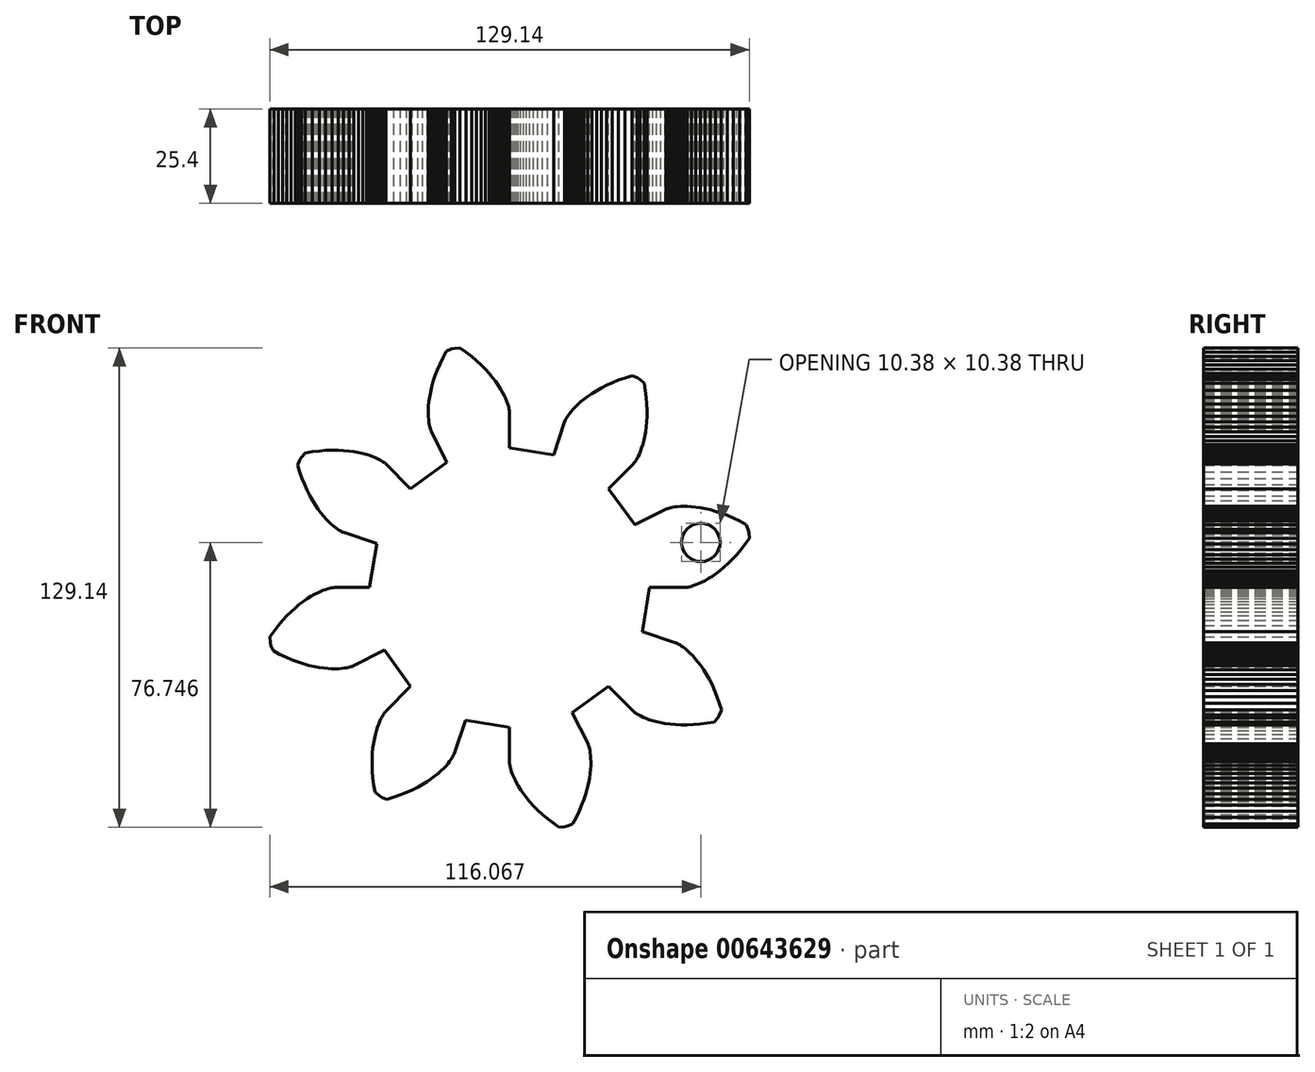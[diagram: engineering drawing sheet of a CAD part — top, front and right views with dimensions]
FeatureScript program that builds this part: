
annotation { "Feature Type Name" : "Feature", "Feature Type Description" : "" }
export const myFeature = defineFeature(function(context is Context, id is Id, definition is map)
    precondition{}
    {
        {
            var Q0;
            Q0=qCreatedBy(makeId("Front.planeOp"),FACE);
            var sketch = newSketch(context, id + "F0", { "sketchPlane" : qUnion([Q0])});
            skLineSegment(sketch, "E0", {"start": v(37.7, 0) * mm, "end": v(47.16, 0) * mm});
            skLineSegment(sketch, "E1", {"start": v(47.16, 0) * mm, "end": v(47.24, 0) * mm});
            skLineSegment(sketch, "E2", {"start": v(47.24, 0) * mm, "end": v(47.4, 0.02) * mm});
            skLineSegment(sketch, "E3", {"start": v(47.4, 0.02) * mm, "end": v(47.67, 0.05) * mm});
            skLineSegment(sketch, "E4", {"start": v(47.67, 0.05) * mm, "end": v(48, 0.11) * mm});
            skLineSegment(sketch, "E5", {"start": v(48, 0.11) * mm, "end": v(48.44, 0.2) * mm});
            skLineSegment(sketch, "E6", {"start": v(48.44, 0.2) * mm, "end": v(48.95, 0.34) * mm});
            skLineSegment(sketch, "E7", {"start": v(48.95, 0.34) * mm, "end": v(49.54, 0.52) * mm});
            skLineSegment(sketch, "E8", {"start": v(49.54, 0.52) * mm, "end": v(50.21, 0.76) * mm});
            skLineSegment(sketch, "E9", {"start": v(50.21, 0.76) * mm, "end": v(50.95, 1.07) * mm});
            skLineSegment(sketch, "E10", {"start": v(50.95, 1.07) * mm, "end": v(51.76, 1.44) * mm});
            skLineSegment(sketch, "E11", {"start": v(51.76, 1.44) * mm, "end": v(52.63, 1.89) * mm});
            skLineSegment(sketch, "E12", {"start": v(52.63, 1.89) * mm, "end": v(53.55, 2.42) * mm});
            skLineSegment(sketch, "E13", {"start": v(53.55, 2.42) * mm, "end": v(54.53, 3.04) * mm});
            skLineSegment(sketch, "E14", {"start": v(54.53, 3.04) * mm, "end": v(55.56, 3.75) * mm});
            skLineSegment(sketch, "E15", {"start": v(55.56, 3.75) * mm, "end": v(56.62, 4.56) * mm});
            skLineSegment(sketch, "E16", {"start": v(56.62, 4.56) * mm, "end": v(57.72, 5.47) * mm});
            skLineSegment(sketch, "E17", {"start": v(57.72, 5.47) * mm, "end": v(58.84, 6.49) * mm});
            skLineSegment(sketch, "E18", {"start": v(58.84, 6.49) * mm, "end": v(59.98, 7.62) * mm});
            skLineSegment(sketch, "E19", {"start": v(59.98, 7.62) * mm, "end": v(61.13, 8.87) * mm});
            skLineSegment(sketch, "E20", {"start": v(61.13, 8.87) * mm, "end": v(62.29, 10.23) * mm});
            skLineSegment(sketch, "E21", {"start": v(62.29, 10.23) * mm, "end": v(63.44, 11.71) * mm});
            skLineSegment(sketch, "E22", {"start": v(63.44, 11.71) * mm, "end": v(64.57, 13.32) * mm});
            skLineSegment(sketch, "E23", {"start": v(64.57, 13.32) * mm, "end": v(64.48, 14.77) * mm});
            skLineSegment(sketch, "E24", {"start": v(64.48, 14.77) * mm, "end": v(64.26, 15.67) * mm});
            skLineSegment(sketch, "E25", {"start": v(64.26, 15.67) * mm, "end": v(63.7, 17.01) * mm});
            skLineSegment(sketch, "E26", {"start": v(63.7, 17.01) * mm, "end": v(61.96, 17.94) * mm});
            skLineSegment(sketch, "E27", {"start": v(61.96, 17.94) * mm, "end": v(60.27, 18.75) * mm});
            skLineSegment(sketch, "E28", {"start": v(60.27, 18.75) * mm, "end": v(58.63, 19.45) * mm});
            skLineSegment(sketch, "E29", {"start": v(58.63, 19.45) * mm, "end": v(57.04, 20.05) * mm});
            skLineSegment(sketch, "E30", {"start": v(57.04, 20.05) * mm, "end": v(55.52, 20.55) * mm});
            skLineSegment(sketch, "E31", {"start": v(55.52, 20.55) * mm, "end": v(54.06, 20.96) * mm});
            skLineSegment(sketch, "E32", {"start": v(54.06, 20.96) * mm, "end": v(52.67, 21.29) * mm});
            skLineSegment(sketch, "E33", {"start": v(52.67, 21.29) * mm, "end": v(51.35, 21.53) * mm});
            skLineSegment(sketch, "E34", {"start": v(51.35, 21.53) * mm, "end": v(50.12, 21.7) * mm});
            skLineSegment(sketch, "E35", {"start": v(50.12, 21.7) * mm, "end": v(48.96, 21.82) * mm});
            skLineSegment(sketch, "E36", {"start": v(48.96, 21.82) * mm, "end": v(47.9, 21.88) * mm});
            skLineSegment(sketch, "E37", {"start": v(47.9, 21.88) * mm, "end": v(46.92, 21.9) * mm});
            skLineSegment(sketch, "E38", {"start": v(46.92, 21.9) * mm, "end": v(46.03, 21.87) * mm});
            skLineSegment(sketch, "E39", {"start": v(46.03, 21.87) * mm, "end": v(45.24, 21.8) * mm});
            skLineSegment(sketch, "E40", {"start": v(45.24, 21.8) * mm, "end": v(44.53, 21.72) * mm});
            skLineSegment(sketch, "E41", {"start": v(44.53, 21.72) * mm, "end": v(43.92, 21.62) * mm});
            skLineSegment(sketch, "E42", {"start": v(43.92, 21.62) * mm, "end": v(43.4, 21.51) * mm});
            skLineSegment(sketch, "E43", {"start": v(43.4, 21.51) * mm, "end": v(42.98, 21.4) * mm});
            skLineSegment(sketch, "E44", {"start": v(42.98, 21.4) * mm, "end": v(42.64, 21.3) * mm});
            skLineSegment(sketch, "E45", {"start": v(42.64, 21.3) * mm, "end": v(42.4, 21.22) * mm});
            skLineSegment(sketch, "E46", {"start": v(42.4, 21.22) * mm, "end": v(42.24, 21.15) * mm});
            skLineSegment(sketch, "E47", {"start": v(42.24, 21.15) * mm, "end": v(42.16, 21.12) * mm});
            skLineSegment(sketch, "E48", {"start": v(42.16, 21.12) * mm, "end": v(33.71, 16.89) * mm});
            skLineSegment(sketch, "E49", {"start": v(33.71, 16.89) * mm, "end": v(26.66, 26.66) * mm});
            skLineSegment(sketch, "E50", {"start": v(26.66, 26.66) * mm, "end": v(33.34, 33.34) * mm});
            skLineSegment(sketch, "E51", {"start": v(33.34, 33.34) * mm, "end": v(33.4, 33.4) * mm});
            skLineSegment(sketch, "E52", {"start": v(33.4, 33.4) * mm, "end": v(33.5, 33.53) * mm});
            skLineSegment(sketch, "E53", {"start": v(33.5, 33.53) * mm, "end": v(33.67, 33.74) * mm});
            skLineSegment(sketch, "E54", {"start": v(33.67, 33.74) * mm, "end": v(33.87, 34.03) * mm});
            skLineSegment(sketch, "E55", {"start": v(33.87, 34.03) * mm, "end": v(34.1, 34.4) * mm});
            skLineSegment(sketch, "E56", {"start": v(34.1, 34.4) * mm, "end": v(34.37, 34.85) * mm});
            skLineSegment(sketch, "E57", {"start": v(34.37, 34.85) * mm, "end": v(34.66, 35.4) * mm});
            skLineSegment(sketch, "E58", {"start": v(34.66, 35.4) * mm, "end": v(34.97, 36.04) * mm});
            skLineSegment(sketch, "E59", {"start": v(34.97, 36.04) * mm, "end": v(35.27, 36.78) * mm});
            skLineSegment(sketch, "E60", {"start": v(35.27, 36.78) * mm, "end": v(35.58, 37.62) * mm});
            skLineSegment(sketch, "E61", {"start": v(35.58, 37.62) * mm, "end": v(35.88, 38.55) * mm});
            skLineSegment(sketch, "E62", {"start": v(35.88, 38.55) * mm, "end": v(36.16, 39.58) * mm});
            skLineSegment(sketch, "E63", {"start": v(36.16, 39.58) * mm, "end": v(36.41, 40.7) * mm});
            skLineSegment(sketch, "E64", {"start": v(36.41, 40.7) * mm, "end": v(36.64, 41.93) * mm});
            skLineSegment(sketch, "E65", {"start": v(36.64, 41.93) * mm, "end": v(36.82, 43.26) * mm});
            skLineSegment(sketch, "E66", {"start": v(36.82, 43.26) * mm, "end": v(36.95, 44.68) * mm});
            skLineSegment(sketch, "E67", {"start": v(36.95, 44.68) * mm, "end": v(37.02, 46.2) * mm});
            skLineSegment(sketch, "E68", {"start": v(37.02, 46.2) * mm, "end": v(37.03, 47.8) * mm});
            skLineSegment(sketch, "E69", {"start": v(37.03, 47.8) * mm, "end": v(36.96, 49.5) * mm});
            skLineSegment(sketch, "E70", {"start": v(36.96, 49.5) * mm, "end": v(36.81, 51.28) * mm});
            skLineSegment(sketch, "E71", {"start": v(36.81, 51.28) * mm, "end": v(36.57, 53.14) * mm});
            skLineSegment(sketch, "E72", {"start": v(36.57, 53.14) * mm, "end": v(36.24, 55.08) * mm});
            skLineSegment(sketch, "E73", {"start": v(36.24, 55.08) * mm, "end": v(35.15, 56.04) * mm});
            skLineSegment(sketch, "E74", {"start": v(35.15, 56.04) * mm, "end": v(34.36, 56.52) * mm});
            skLineSegment(sketch, "E75", {"start": v(34.36, 56.52) * mm, "end": v(33.01, 57.07) * mm});
            skLineSegment(sketch, "E76", {"start": v(33.01, 57.07) * mm, "end": v(31.13, 56.5) * mm});
            skLineSegment(sketch, "E77", {"start": v(31.13, 56.5) * mm, "end": v(29.36, 55.88) * mm});
            skLineSegment(sketch, "E78", {"start": v(29.36, 55.88) * mm, "end": v(27.7, 55.21) * mm});
            skLineSegment(sketch, "E79", {"start": v(27.7, 55.21) * mm, "end": v(26.16, 54.51) * mm});
            skLineSegment(sketch, "E80", {"start": v(26.16, 54.51) * mm, "end": v(24.72, 53.79) * mm});
            skLineSegment(sketch, "E81", {"start": v(24.72, 53.79) * mm, "end": v(23.4, 53.04) * mm});
            skLineSegment(sketch, "E82", {"start": v(23.4, 53.04) * mm, "end": v(22.2, 52.3) * mm});
            skLineSegment(sketch, "E83", {"start": v(22.2, 52.3) * mm, "end": v(21.09, 51.54) * mm});
            skLineSegment(sketch, "E84", {"start": v(21.09, 51.54) * mm, "end": v(20.09, 50.79) * mm});
            skLineSegment(sketch, "E85", {"start": v(20.09, 50.79) * mm, "end": v(19.2, 50.05) * mm});
            skLineSegment(sketch, "E86", {"start": v(19.2, 50.05) * mm, "end": v(18.4, 49.34) * mm});
            skLineSegment(sketch, "E87", {"start": v(18.4, 49.34) * mm, "end": v(17.7, 48.66) * mm});
            skLineSegment(sketch, "E88", {"start": v(17.7, 48.66) * mm, "end": v(17.09, 48.01) * mm});
            skLineSegment(sketch, "E89", {"start": v(17.09, 48.01) * mm, "end": v(16.57, 47.4) * mm});
            skLineSegment(sketch, "E90", {"start": v(16.57, 47.4) * mm, "end": v(16.13, 46.85) * mm});
            skLineSegment(sketch, "E91", {"start": v(16.13, 46.85) * mm, "end": v(15.77, 46.34) * mm});
            skLineSegment(sketch, "E92", {"start": v(15.77, 46.34) * mm, "end": v(15.48, 45.9) * mm});
            skLineSegment(sketch, "E93", {"start": v(15.48, 45.9) * mm, "end": v(15.25, 45.52) * mm});
            skLineSegment(sketch, "E94", {"start": v(15.25, 45.52) * mm, "end": v(15.09, 45.21) * mm});
            skLineSegment(sketch, "E95", {"start": v(15.09, 45.21) * mm, "end": v(14.98, 44.98) * mm});
            skLineSegment(sketch, "E96", {"start": v(14.98, 44.98) * mm, "end": v(14.9, 44.82) * mm});
            skLineSegment(sketch, "E97", {"start": v(14.9, 44.82) * mm, "end": v(14.88, 44.75) * mm});
            skLineSegment(sketch, "E98", {"start": v(14.88, 44.75) * mm, "end": v(11.9, 35.78) * mm});
            skLineSegment(sketch, "E99", {"start": v(11.9, 35.78) * mm, "end": v(0, 37.7) * mm});
            skLineSegment(sketch, "E100", {"start": v(0, 37.7) * mm, "end": v(0, 47.16) * mm});
            skLineSegment(sketch, "E101", {"start": v(0, 47.16) * mm, "end": v(0, 47.24) * mm});
            skLineSegment(sketch, "E102", {"start": v(0, 47.24) * mm, "end": v(-0.02, 47.4) * mm});
            skLineSegment(sketch, "E103", {"start": v(-0.02, 47.4) * mm, "end": v(-0.05, 47.67) * mm});
            skLineSegment(sketch, "E104", {"start": v(-0.05, 47.67) * mm, "end": v(-0.11, 48) * mm});
            skLineSegment(sketch, "E105", {"start": v(-0.11, 48) * mm, "end": v(-0.2, 48.44) * mm});
            skLineSegment(sketch, "E106", {"start": v(-0.2, 48.44) * mm, "end": v(-0.34, 48.95) * mm});
            skLineSegment(sketch, "E107", {"start": v(-0.34, 48.95) * mm, "end": v(-0.52, 49.54) * mm});
            skLineSegment(sketch, "E108", {"start": v(-0.52, 49.54) * mm, "end": v(-0.76, 50.21) * mm});
            skLineSegment(sketch, "E109", {"start": v(-0.76, 50.21) * mm, "end": v(-1.07, 50.95) * mm});
            skLineSegment(sketch, "E110", {"start": v(-1.07, 50.95) * mm, "end": v(-1.44, 51.76) * mm});
            skLineSegment(sketch, "E111", {"start": v(-1.44, 51.76) * mm, "end": v(-1.89, 52.63) * mm});
            skLineSegment(sketch, "E112", {"start": v(-1.89, 52.63) * mm, "end": v(-2.42, 53.55) * mm});
            skLineSegment(sketch, "E113", {"start": v(-2.42, 53.55) * mm, "end": v(-3.04, 54.53) * mm});
            skLineSegment(sketch, "E114", {"start": v(-3.04, 54.53) * mm, "end": v(-3.75, 55.56) * mm});
            skLineSegment(sketch, "E115", {"start": v(-3.75, 55.56) * mm, "end": v(-4.56, 56.62) * mm});
            skLineSegment(sketch, "E116", {"start": v(-4.56, 56.62) * mm, "end": v(-5.47, 57.72) * mm});
            skLineSegment(sketch, "E117", {"start": v(-5.47, 57.72) * mm, "end": v(-6.49, 58.84) * mm});
            skLineSegment(sketch, "E118", {"start": v(-6.49, 58.84) * mm, "end": v(-7.62, 59.98) * mm});
            skLineSegment(sketch, "E119", {"start": v(-7.62, 59.98) * mm, "end": v(-8.87, 61.13) * mm});
            skLineSegment(sketch, "E120", {"start": v(-8.87, 61.13) * mm, "end": v(-10.23, 62.29) * mm});
            skLineSegment(sketch, "E121", {"start": v(-10.23, 62.29) * mm, "end": v(-11.71, 63.44) * mm});
            skLineSegment(sketch, "E122", {"start": v(-11.71, 63.44) * mm, "end": v(-13.32, 64.57) * mm});
            skLineSegment(sketch, "E123", {"start": v(-13.32, 64.57) * mm, "end": v(-14.77, 64.48) * mm});
            skLineSegment(sketch, "E124", {"start": v(-14.77, 64.48) * mm, "end": v(-15.67, 64.26) * mm});
            skLineSegment(sketch, "E125", {"start": v(-15.67, 64.26) * mm, "end": v(-17.01, 63.7) * mm});
            skLineSegment(sketch, "E126", {"start": v(-17.01, 63.7) * mm, "end": v(-17.94, 61.96) * mm});
            skLineSegment(sketch, "E127", {"start": v(-17.94, 61.96) * mm, "end": v(-18.75, 60.27) * mm});
            skLineSegment(sketch, "E128", {"start": v(-18.75, 60.27) * mm, "end": v(-19.45, 58.63) * mm});
            skLineSegment(sketch, "E129", {"start": v(-19.45, 58.63) * mm, "end": v(-20.05, 57.04) * mm});
            skLineSegment(sketch, "E130", {"start": v(-20.05, 57.04) * mm, "end": v(-20.55, 55.52) * mm});
            skLineSegment(sketch, "E131", {"start": v(-20.55, 55.52) * mm, "end": v(-20.96, 54.06) * mm});
            skLineSegment(sketch, "E132", {"start": v(-20.96, 54.06) * mm, "end": v(-21.29, 52.67) * mm});
            skLineSegment(sketch, "E133", {"start": v(-21.29, 52.67) * mm, "end": v(-21.53, 51.35) * mm});
            skLineSegment(sketch, "E134", {"start": v(-21.53, 51.35) * mm, "end": v(-21.7, 50.12) * mm});
            skLineSegment(sketch, "E135", {"start": v(-21.7, 50.12) * mm, "end": v(-21.82, 48.96) * mm});
            skLineSegment(sketch, "E136", {"start": v(-21.82, 48.96) * mm, "end": v(-21.88, 47.9) * mm});
            skLineSegment(sketch, "E137", {"start": v(-21.88, 47.9) * mm, "end": v(-21.9, 46.92) * mm});
            skLineSegment(sketch, "E138", {"start": v(-21.9, 46.92) * mm, "end": v(-21.87, 46.03) * mm});
            skLineSegment(sketch, "E139", {"start": v(-21.87, 46.03) * mm, "end": v(-21.8, 45.24) * mm});
            skLineSegment(sketch, "E140", {"start": v(-21.8, 45.24) * mm, "end": v(-21.72, 44.53) * mm});
            skLineSegment(sketch, "E141", {"start": v(-21.72, 44.53) * mm, "end": v(-21.62, 43.92) * mm});
            skLineSegment(sketch, "E142", {"start": v(-21.62, 43.92) * mm, "end": v(-21.51, 43.4) * mm});
            skLineSegment(sketch, "E143", {"start": v(-21.51, 43.4) * mm, "end": v(-21.4, 42.98) * mm});
            skLineSegment(sketch, "E144", {"start": v(-21.4, 42.98) * mm, "end": v(-21.3, 42.64) * mm});
            skLineSegment(sketch, "E145", {"start": v(-21.3, 42.64) * mm, "end": v(-21.22, 42.4) * mm});
            skLineSegment(sketch, "E146", {"start": v(-21.22, 42.4) * mm, "end": v(-21.15, 42.24) * mm});
            skLineSegment(sketch, "E147", {"start": v(-21.15, 42.24) * mm, "end": v(-21.12, 42.16) * mm});
            skLineSegment(sketch, "E148", {"start": v(-21.12, 42.16) * mm, "end": v(-16.89, 33.71) * mm});
            skLineSegment(sketch, "E149", {"start": v(-16.89, 33.71) * mm, "end": v(-26.66, 26.66) * mm});
            skLineSegment(sketch, "E150", {"start": v(-26.66, 26.66) * mm, "end": v(-33.34, 33.34) * mm});
            skLineSegment(sketch, "E151", {"start": v(-33.34, 33.34) * mm, "end": v(-33.4, 33.4) * mm});
            skLineSegment(sketch, "E152", {"start": v(-33.4, 33.4) * mm, "end": v(-33.53, 33.5) * mm});
            skLineSegment(sketch, "E153", {"start": v(-33.53, 33.5) * mm, "end": v(-33.74, 33.67) * mm});
            skLineSegment(sketch, "E154", {"start": v(-33.74, 33.67) * mm, "end": v(-34.03, 33.87) * mm});
            skLineSegment(sketch, "E155", {"start": v(-34.03, 33.87) * mm, "end": v(-34.4, 34.1) * mm});
            skLineSegment(sketch, "E156", {"start": v(-34.4, 34.1) * mm, "end": v(-34.85, 34.37) * mm});
            skLineSegment(sketch, "E157", {"start": v(-34.85, 34.37) * mm, "end": v(-35.4, 34.66) * mm});
            skLineSegment(sketch, "E158", {"start": v(-35.4, 34.66) * mm, "end": v(-36.04, 34.97) * mm});
            skLineSegment(sketch, "E159", {"start": v(-36.04, 34.97) * mm, "end": v(-36.78, 35.27) * mm});
            skLineSegment(sketch, "E160", {"start": v(-36.78, 35.27) * mm, "end": v(-37.61, 35.58) * mm});
            skLineSegment(sketch, "E161", {"start": v(-37.61, 35.58) * mm, "end": v(-38.55, 35.88) * mm});
            skLineSegment(sketch, "E162", {"start": v(-38.55, 35.88) * mm, "end": v(-39.58, 36.16) * mm});
            skLineSegment(sketch, "E163", {"start": v(-39.58, 36.16) * mm, "end": v(-40.7, 36.41) * mm});
            skLineSegment(sketch, "E164", {"start": v(-40.7, 36.41) * mm, "end": v(-41.93, 36.64) * mm});
            skLineSegment(sketch, "E165", {"start": v(-41.93, 36.64) * mm, "end": v(-43.26, 36.82) * mm});
            skLineSegment(sketch, "E166", {"start": v(-43.26, 36.82) * mm, "end": v(-44.68, 36.95) * mm});
            skLineSegment(sketch, "E167", {"start": v(-44.68, 36.95) * mm, "end": v(-46.2, 37.02) * mm});
            skLineSegment(sketch, "E168", {"start": v(-46.2, 37.02) * mm, "end": v(-47.8, 37.03) * mm});
            skLineSegment(sketch, "E169", {"start": v(-47.8, 37.03) * mm, "end": v(-49.5, 36.96) * mm});
            skLineSegment(sketch, "E170", {"start": v(-49.5, 36.96) * mm, "end": v(-51.28, 36.81) * mm});
            skLineSegment(sketch, "E171", {"start": v(-51.28, 36.81) * mm, "end": v(-53.14, 36.57) * mm});
            skLineSegment(sketch, "E172", {"start": v(-53.14, 36.57) * mm, "end": v(-55.08, 36.24) * mm});
            skLineSegment(sketch, "E173", {"start": v(-55.08, 36.24) * mm, "end": v(-56.04, 35.15) * mm});
            skLineSegment(sketch, "E174", {"start": v(-56.04, 35.15) * mm, "end": v(-56.52, 34.36) * mm});
            skLineSegment(sketch, "E175", {"start": v(-56.52, 34.36) * mm, "end": v(-57.07, 33.01) * mm});
            skLineSegment(sketch, "E176", {"start": v(-57.07, 33.01) * mm, "end": v(-56.5, 31.13) * mm});
            skLineSegment(sketch, "E177", {"start": v(-56.5, 31.13) * mm, "end": v(-55.88, 29.36) * mm});
            skLineSegment(sketch, "E178", {"start": v(-55.88, 29.36) * mm, "end": v(-55.21, 27.7) * mm});
            skLineSegment(sketch, "E179", {"start": v(-55.21, 27.7) * mm, "end": v(-54.51, 26.16) * mm});
            skLineSegment(sketch, "E180", {"start": v(-54.51, 26.16) * mm, "end": v(-53.79, 24.72) * mm});
            skLineSegment(sketch, "E181", {"start": v(-53.79, 24.72) * mm, "end": v(-53.04, 23.4) * mm});
            skLineSegment(sketch, "E182", {"start": v(-53.04, 23.4) * mm, "end": v(-52.3, 22.2) * mm});
            skLineSegment(sketch, "E183", {"start": v(-52.3, 22.2) * mm, "end": v(-51.54, 21.09) * mm});
            skLineSegment(sketch, "E184", {"start": v(-51.54, 21.09) * mm, "end": v(-50.79, 20.09) * mm});
            skLineSegment(sketch, "E185", {"start": v(-50.79, 20.09) * mm, "end": v(-50.05, 19.2) * mm});
            skLineSegment(sketch, "E186", {"start": v(-50.05, 19.2) * mm, "end": v(-49.34, 18.4) * mm});
            skLineSegment(sketch, "E187", {"start": v(-49.34, 18.4) * mm, "end": v(-48.66, 17.7) * mm});
            skLineSegment(sketch, "E188", {"start": v(-48.66, 17.7) * mm, "end": v(-48.01, 17.09) * mm});
            skLineSegment(sketch, "E189", {"start": v(-48.01, 17.09) * mm, "end": v(-47.4, 16.57) * mm});
            skLineSegment(sketch, "E190", {"start": v(-47.4, 16.57) * mm, "end": v(-46.85, 16.13) * mm});
            skLineSegment(sketch, "E191", {"start": v(-46.85, 16.13) * mm, "end": v(-46.34, 15.77) * mm});
            skLineSegment(sketch, "E192", {"start": v(-46.34, 15.77) * mm, "end": v(-45.9, 15.48) * mm});
            skLineSegment(sketch, "E193", {"start": v(-45.9, 15.48) * mm, "end": v(-45.52, 15.25) * mm});
            skLineSegment(sketch, "E194", {"start": v(-45.52, 15.25) * mm, "end": v(-45.21, 15.09) * mm});
            skLineSegment(sketch, "E195", {"start": v(-45.21, 15.09) * mm, "end": v(-44.98, 14.98) * mm});
            skLineSegment(sketch, "E196", {"start": v(-44.98, 14.98) * mm, "end": v(-44.82, 14.9) * mm});
            skLineSegment(sketch, "E197", {"start": v(-44.82, 14.9) * mm, "end": v(-44.75, 14.88) * mm});
            skLineSegment(sketch, "E198", {"start": v(-44.75, 14.88) * mm, "end": v(-35.78, 11.9) * mm});
            skLineSegment(sketch, "E199", {"start": v(-35.78, 11.9) * mm, "end": v(-37.7, 0) * mm});
            skLineSegment(sketch, "E200", {"start": v(-37.7, 0) * mm, "end": v(-47.16, 0) * mm});
            skLineSegment(sketch, "E201", {"start": v(-47.16, 0) * mm, "end": v(-47.24, 0) * mm});
            skLineSegment(sketch, "E202", {"start": v(-47.24, 0) * mm, "end": v(-47.4, -0.02) * mm});
            skLineSegment(sketch, "E203", {"start": v(-47.4, -0.02) * mm, "end": v(-47.66, -0.05) * mm});
            skLineSegment(sketch, "E204", {"start": v(-47.66, -0.05) * mm, "end": v(-48, -0.11) * mm});
            skLineSegment(sketch, "E205", {"start": v(-48, -0.11) * mm, "end": v(-48.44, -0.2) * mm});
            skLineSegment(sketch, "E206", {"start": v(-48.44, -0.2) * mm, "end": v(-48.95, -0.34) * mm});
            skLineSegment(sketch, "E207", {"start": v(-48.95, -0.34) * mm, "end": v(-49.54, -0.52) * mm});
            skLineSegment(sketch, "E208", {"start": v(-49.54, -0.52) * mm, "end": v(-50.21, -0.76) * mm});
            skLineSegment(sketch, "E209", {"start": v(-50.21, -0.76) * mm, "end": v(-50.95, -1.07) * mm});
            skLineSegment(sketch, "E210", {"start": v(-50.95, -1.07) * mm, "end": v(-51.76, -1.44) * mm});
            skLineSegment(sketch, "E211", {"start": v(-51.76, -1.44) * mm, "end": v(-52.63, -1.89) * mm});
            skLineSegment(sketch, "E212", {"start": v(-52.63, -1.89) * mm, "end": v(-53.55, -2.42) * mm});
            skLineSegment(sketch, "E213", {"start": v(-53.55, -2.42) * mm, "end": v(-54.53, -3.04) * mm});
            skLineSegment(sketch, "E214", {"start": v(-54.53, -3.04) * mm, "end": v(-55.56, -3.75) * mm});
            skLineSegment(sketch, "E215", {"start": v(-55.56, -3.75) * mm, "end": v(-56.62, -4.56) * mm});
            skLineSegment(sketch, "E216", {"start": v(-56.62, -4.56) * mm, "end": v(-57.72, -5.47) * mm});
            skLineSegment(sketch, "E217", {"start": v(-57.72, -5.47) * mm, "end": v(-58.84, -6.49) * mm});
            skLineSegment(sketch, "E218", {"start": v(-58.84, -6.49) * mm, "end": v(-59.98, -7.62) * mm});
            skLineSegment(sketch, "E219", {"start": v(-59.98, -7.62) * mm, "end": v(-61.13, -8.87) * mm});
            skLineSegment(sketch, "E220", {"start": v(-61.13, -8.87) * mm, "end": v(-62.29, -10.23) * mm});
            skLineSegment(sketch, "E221", {"start": v(-62.29, -10.23) * mm, "end": v(-63.44, -11.71) * mm});
            skLineSegment(sketch, "E222", {"start": v(-63.44, -11.71) * mm, "end": v(-64.57, -13.32) * mm});
            skLineSegment(sketch, "E223", {"start": v(-64.57, -13.32) * mm, "end": v(-64.48, -14.77) * mm});
            skLineSegment(sketch, "E224", {"start": v(-64.48, -14.77) * mm, "end": v(-64.26, -15.67) * mm});
            skLineSegment(sketch, "E225", {"start": v(-64.26, -15.67) * mm, "end": v(-63.7, -17.01) * mm});
            skLineSegment(sketch, "E226", {"start": v(-63.7, -17.01) * mm, "end": v(-61.96, -17.94) * mm});
            skLineSegment(sketch, "E227", {"start": v(-61.96, -17.94) * mm, "end": v(-60.27, -18.75) * mm});
            skLineSegment(sketch, "E228", {"start": v(-60.27, -18.75) * mm, "end": v(-58.63, -19.45) * mm});
            skLineSegment(sketch, "E229", {"start": v(-58.63, -19.45) * mm, "end": v(-57.04, -20.05) * mm});
            skLineSegment(sketch, "E230", {"start": v(-57.04, -20.05) * mm, "end": v(-55.52, -20.55) * mm});
            skLineSegment(sketch, "E231", {"start": v(-55.52, -20.55) * mm, "end": v(-54.06, -20.96) * mm});
            skLineSegment(sketch, "E232", {"start": v(-54.06, -20.96) * mm, "end": v(-52.67, -21.29) * mm});
            skLineSegment(sketch, "E233", {"start": v(-52.67, -21.29) * mm, "end": v(-51.35, -21.53) * mm});
            skLineSegment(sketch, "E234", {"start": v(-51.35, -21.53) * mm, "end": v(-50.12, -21.7) * mm});
            skLineSegment(sketch, "E235", {"start": v(-50.12, -21.7) * mm, "end": v(-48.96, -21.82) * mm});
            skLineSegment(sketch, "E236", {"start": v(-48.96, -21.82) * mm, "end": v(-47.9, -21.88) * mm});
            skLineSegment(sketch, "E237", {"start": v(-47.9, -21.88) * mm, "end": v(-46.92, -21.9) * mm});
            skLineSegment(sketch, "E238", {"start": v(-46.92, -21.9) * mm, "end": v(-46.03, -21.87) * mm});
            skLineSegment(sketch, "E239", {"start": v(-46.03, -21.87) * mm, "end": v(-45.24, -21.8) * mm});
            skLineSegment(sketch, "E240", {"start": v(-45.24, -21.8) * mm, "end": v(-44.53, -21.72) * mm});
            skLineSegment(sketch, "E241", {"start": v(-44.53, -21.72) * mm, "end": v(-43.92, -21.62) * mm});
            skLineSegment(sketch, "E242", {"start": v(-43.92, -21.62) * mm, "end": v(-43.4, -21.51) * mm});
            skLineSegment(sketch, "E243", {"start": v(-43.4, -21.51) * mm, "end": v(-42.98, -21.4) * mm});
            skLineSegment(sketch, "E244", {"start": v(-42.98, -21.4) * mm, "end": v(-42.64, -21.3) * mm});
            skLineSegment(sketch, "E245", {"start": v(-42.64, -21.3) * mm, "end": v(-42.4, -21.22) * mm});
            skLineSegment(sketch, "E246", {"start": v(-42.4, -21.22) * mm, "end": v(-42.24, -21.15) * mm});
            skLineSegment(sketch, "E247", {"start": v(-42.24, -21.15) * mm, "end": v(-42.16, -21.12) * mm});
            skLineSegment(sketch, "E248", {"start": v(-42.16, -21.12) * mm, "end": v(-33.71, -16.89) * mm});
            skLineSegment(sketch, "E249", {"start": v(-33.71, -16.89) * mm, "end": v(-26.66, -26.66) * mm});
            skLineSegment(sketch, "E250", {"start": v(-26.66, -26.66) * mm, "end": v(-33.34, -33.34) * mm});
            skLineSegment(sketch, "E251", {"start": v(-33.34, -33.34) * mm, "end": v(-33.4, -33.4) * mm});
            skLineSegment(sketch, "E252", {"start": v(-33.4, -33.4) * mm, "end": v(-33.5, -33.53) * mm});
            skLineSegment(sketch, "E253", {"start": v(-33.5, -33.53) * mm, "end": v(-33.67, -33.74) * mm});
            skLineSegment(sketch, "E254", {"start": v(-33.67, -33.74) * mm, "end": v(-33.87, -34.03) * mm});
            skLineSegment(sketch, "E255", {"start": v(-33.87, -34.03) * mm, "end": v(-34.1, -34.4) * mm});
            skLineSegment(sketch, "E256", {"start": v(-34.1, -34.4) * mm, "end": v(-34.37, -34.85) * mm});
            skLineSegment(sketch, "E257", {"start": v(-34.37, -34.85) * mm, "end": v(-34.66, -35.4) * mm});
            skLineSegment(sketch, "E258", {"start": v(-34.66, -35.4) * mm, "end": v(-34.96, -36.04) * mm});
            skLineSegment(sketch, "E259", {"start": v(-34.96, -36.04) * mm, "end": v(-35.27, -36.78) * mm});
            skLineSegment(sketch, "E260", {"start": v(-35.27, -36.78) * mm, "end": v(-35.58, -37.61) * mm});
            skLineSegment(sketch, "E261", {"start": v(-35.58, -37.61) * mm, "end": v(-35.88, -38.55) * mm});
            skLineSegment(sketch, "E262", {"start": v(-35.88, -38.55) * mm, "end": v(-36.16, -39.58) * mm});
            skLineSegment(sketch, "E263", {"start": v(-36.16, -39.58) * mm, "end": v(-36.41, -40.7) * mm});
            skLineSegment(sketch, "E264", {"start": v(-36.41, -40.7) * mm, "end": v(-36.64, -41.93) * mm});
            skLineSegment(sketch, "E265", {"start": v(-36.64, -41.93) * mm, "end": v(-36.82, -43.26) * mm});
            skLineSegment(sketch, "E266", {"start": v(-36.82, -43.26) * mm, "end": v(-36.95, -44.68) * mm});
            skLineSegment(sketch, "E267", {"start": v(-36.95, -44.68) * mm, "end": v(-37.02, -46.2) * mm});
            skLineSegment(sketch, "E268", {"start": v(-37.02, -46.2) * mm, "end": v(-37.03, -47.8) * mm});
            skLineSegment(sketch, "E269", {"start": v(-37.03, -47.8) * mm, "end": v(-36.96, -49.5) * mm});
            skLineSegment(sketch, "E270", {"start": v(-36.96, -49.5) * mm, "end": v(-36.81, -51.28) * mm});
            skLineSegment(sketch, "E271", {"start": v(-36.81, -51.28) * mm, "end": v(-36.57, -53.14) * mm});
            skLineSegment(sketch, "E272", {"start": v(-36.57, -53.14) * mm, "end": v(-36.24, -55.08) * mm});
            skLineSegment(sketch, "E273", {"start": v(-36.24, -55.08) * mm, "end": v(-35.15, -56.04) * mm});
            skLineSegment(sketch, "E274", {"start": v(-35.15, -56.04) * mm, "end": v(-34.36, -56.52) * mm});
            skLineSegment(sketch, "E275", {"start": v(-34.36, -56.52) * mm, "end": v(-33.01, -57.07) * mm});
            skLineSegment(sketch, "E276", {"start": v(-33.01, -57.07) * mm, "end": v(-31.13, -56.5) * mm});
            skLineSegment(sketch, "E277", {"start": v(-31.13, -56.5) * mm, "end": v(-29.36, -55.88) * mm});
            skLineSegment(sketch, "E278", {"start": v(-29.36, -55.88) * mm, "end": v(-27.7, -55.21) * mm});
            skLineSegment(sketch, "E279", {"start": v(-27.7, -55.21) * mm, "end": v(-26.16, -54.51) * mm});
            skLineSegment(sketch, "E280", {"start": v(-26.16, -54.51) * mm, "end": v(-24.72, -53.79) * mm});
            skLineSegment(sketch, "E281", {"start": v(-24.72, -53.79) * mm, "end": v(-23.4, -53.04) * mm});
            skLineSegment(sketch, "E282", {"start": v(-23.4, -53.04) * mm, "end": v(-22.2, -52.3) * mm});
            skLineSegment(sketch, "E283", {"start": v(-22.2, -52.3) * mm, "end": v(-21.09, -51.54) * mm});
            skLineSegment(sketch, "E284", {"start": v(-21.09, -51.54) * mm, "end": v(-20.09, -50.79) * mm});
            skLineSegment(sketch, "E285", {"start": v(-20.09, -50.79) * mm, "end": v(-19.2, -50.05) * mm});
            skLineSegment(sketch, "E286", {"start": v(-19.2, -50.05) * mm, "end": v(-18.4, -49.34) * mm});
            skLineSegment(sketch, "E287", {"start": v(-18.4, -49.34) * mm, "end": v(-17.7, -48.66) * mm});
            skLineSegment(sketch, "E288", {"start": v(-17.7, -48.66) * mm, "end": v(-17.09, -48.01) * mm});
            skLineSegment(sketch, "E289", {"start": v(-17.09, -48.01) * mm, "end": v(-16.57, -47.4) * mm});
            skLineSegment(sketch, "E290", {"start": v(-16.57, -47.4) * mm, "end": v(-16.13, -46.85) * mm});
            skLineSegment(sketch, "E291", {"start": v(-16.13, -46.85) * mm, "end": v(-15.77, -46.34) * mm});
            skLineSegment(sketch, "E292", {"start": v(-15.77, -46.34) * mm, "end": v(-15.48, -45.9) * mm});
            skLineSegment(sketch, "E293", {"start": v(-15.48, -45.9) * mm, "end": v(-15.25, -45.52) * mm});
            skLineSegment(sketch, "E294", {"start": v(-15.25, -45.52) * mm, "end": v(-15.09, -45.21) * mm});
            skLineSegment(sketch, "E295", {"start": v(-15.09, -45.21) * mm, "end": v(-14.97, -44.98) * mm});
            skLineSegment(sketch, "E296", {"start": v(-14.97, -44.98) * mm, "end": v(-14.9, -44.82) * mm});
            skLineSegment(sketch, "E297", {"start": v(-14.9, -44.82) * mm, "end": v(-14.88, -44.75) * mm});
            skLineSegment(sketch, "E298", {"start": v(-14.88, -44.75) * mm, "end": v(-11.9, -35.78) * mm});
            skLineSegment(sketch, "E299", {"start": v(-11.9, -35.78) * mm, "end": v(0, -37.7) * mm});
            skLineSegment(sketch, "E300", {"start": v(0, -37.7) * mm, "end": v(0, -47.16) * mm});
            skLineSegment(sketch, "E301", {"start": v(0, -47.16) * mm, "end": v(0, -47.24) * mm});
            skLineSegment(sketch, "E302", {"start": v(0, -47.24) * mm, "end": v(0.02, -47.4) * mm});
            skLineSegment(sketch, "E303", {"start": v(0.02, -47.4) * mm, "end": v(0.05, -47.66) * mm});
            skLineSegment(sketch, "E304", {"start": v(0.05, -47.66) * mm, "end": v(0.11, -48) * mm});
            skLineSegment(sketch, "E305", {"start": v(0.11, -48) * mm, "end": v(0.2, -48.44) * mm});
            skLineSegment(sketch, "E306", {"start": v(0.2, -48.44) * mm, "end": v(0.34, -48.95) * mm});
            skLineSegment(sketch, "E307", {"start": v(0.34, -48.95) * mm, "end": v(0.52, -49.54) * mm});
            skLineSegment(sketch, "E308", {"start": v(0.52, -49.54) * mm, "end": v(0.76, -50.21) * mm});
            skLineSegment(sketch, "E309", {"start": v(0.76, -50.21) * mm, "end": v(1.07, -50.95) * mm});
            skLineSegment(sketch, "E310", {"start": v(1.07, -50.95) * mm, "end": v(1.44, -51.76) * mm});
            skLineSegment(sketch, "E311", {"start": v(1.44, -51.76) * mm, "end": v(1.89, -52.63) * mm});
            skLineSegment(sketch, "E312", {"start": v(1.89, -52.63) * mm, "end": v(2.42, -53.55) * mm});
            skLineSegment(sketch, "E313", {"start": v(2.42, -53.55) * mm, "end": v(3.04, -54.53) * mm});
            skLineSegment(sketch, "E314", {"start": v(3.04, -54.53) * mm, "end": v(3.75, -55.56) * mm});
            skLineSegment(sketch, "E315", {"start": v(3.75, -55.56) * mm, "end": v(4.56, -56.62) * mm});
            skLineSegment(sketch, "E316", {"start": v(4.56, -56.62) * mm, "end": v(5.47, -57.72) * mm});
            skLineSegment(sketch, "E317", {"start": v(5.47, -57.72) * mm, "end": v(6.49, -58.84) * mm});
            skLineSegment(sketch, "E318", {"start": v(6.49, -58.84) * mm, "end": v(7.62, -59.98) * mm});
            skLineSegment(sketch, "E319", {"start": v(7.62, -59.98) * mm, "end": v(8.87, -61.13) * mm});
            skLineSegment(sketch, "E320", {"start": v(8.87, -61.13) * mm, "end": v(10.23, -62.29) * mm});
            skLineSegment(sketch, "E321", {"start": v(10.23, -62.29) * mm, "end": v(11.71, -63.44) * mm});
            skLineSegment(sketch, "E322", {"start": v(11.71, -63.44) * mm, "end": v(13.32, -64.57) * mm});
            skLineSegment(sketch, "E323", {"start": v(13.32, -64.57) * mm, "end": v(14.77, -64.48) * mm});
            skLineSegment(sketch, "E324", {"start": v(14.77, -64.48) * mm, "end": v(15.67, -64.26) * mm});
            skLineSegment(sketch, "E325", {"start": v(15.67, -64.26) * mm, "end": v(17.01, -63.7) * mm});
            skLineSegment(sketch, "E326", {"start": v(17.01, -63.7) * mm, "end": v(17.94, -61.96) * mm});
            skLineSegment(sketch, "E327", {"start": v(17.94, -61.96) * mm, "end": v(18.75, -60.27) * mm});
            skLineSegment(sketch, "E328", {"start": v(18.75, -60.27) * mm, "end": v(19.45, -58.63) * mm});
            skLineSegment(sketch, "E329", {"start": v(19.45, -58.63) * mm, "end": v(20.05, -57.04) * mm});
            skLineSegment(sketch, "E330", {"start": v(20.05, -57.04) * mm, "end": v(20.55, -55.52) * mm});
            skLineSegment(sketch, "E331", {"start": v(20.55, -55.52) * mm, "end": v(20.96, -54.06) * mm});
            skLineSegment(sketch, "E332", {"start": v(20.96, -54.06) * mm, "end": v(21.29, -52.67) * mm});
            skLineSegment(sketch, "E333", {"start": v(21.29, -52.67) * mm, "end": v(21.53, -51.35) * mm});
            skLineSegment(sketch, "E334", {"start": v(21.53, -51.35) * mm, "end": v(21.7, -50.12) * mm});
            skLineSegment(sketch, "E335", {"start": v(21.7, -50.12) * mm, "end": v(21.82, -48.96) * mm});
            skLineSegment(sketch, "E336", {"start": v(21.82, -48.96) * mm, "end": v(21.88, -47.9) * mm});
            skLineSegment(sketch, "E337", {"start": v(21.88, -47.9) * mm, "end": v(21.9, -46.92) * mm});
            skLineSegment(sketch, "E338", {"start": v(21.9, -46.92) * mm, "end": v(21.87, -46.03) * mm});
            skLineSegment(sketch, "E339", {"start": v(21.87, -46.03) * mm, "end": v(21.8, -45.24) * mm});
            skLineSegment(sketch, "E340", {"start": v(21.8, -45.24) * mm, "end": v(21.72, -44.53) * mm});
            skLineSegment(sketch, "E341", {"start": v(21.72, -44.53) * mm, "end": v(21.62, -43.92) * mm});
            skLineSegment(sketch, "E342", {"start": v(21.62, -43.92) * mm, "end": v(21.51, -43.4) * mm});
            skLineSegment(sketch, "E343", {"start": v(21.51, -43.4) * mm, "end": v(21.4, -42.98) * mm});
            skLineSegment(sketch, "E344", {"start": v(21.4, -42.98) * mm, "end": v(21.3, -42.64) * mm});
            skLineSegment(sketch, "E345", {"start": v(21.3, -42.64) * mm, "end": v(21.22, -42.4) * mm});
            skLineSegment(sketch, "E346", {"start": v(21.22, -42.4) * mm, "end": v(21.15, -42.24) * mm});
            skLineSegment(sketch, "E347", {"start": v(21.15, -42.24) * mm, "end": v(21.12, -42.16) * mm});
            skLineSegment(sketch, "E348", {"start": v(21.12, -42.16) * mm, "end": v(16.89, -33.71) * mm});
            skLineSegment(sketch, "E349", {"start": v(16.89, -33.71) * mm, "end": v(26.66, -26.66) * mm});
            skLineSegment(sketch, "E350", {"start": v(26.66, -26.66) * mm, "end": v(33.34, -33.34) * mm});
            skLineSegment(sketch, "E351", {"start": v(33.34, -33.34) * mm, "end": v(33.4, -33.4) * mm});
            skLineSegment(sketch, "E352", {"start": v(33.4, -33.4) * mm, "end": v(33.53, -33.5) * mm});
            skLineSegment(sketch, "E353", {"start": v(33.53, -33.5) * mm, "end": v(33.74, -33.67) * mm});
            skLineSegment(sketch, "E354", {"start": v(33.74, -33.67) * mm, "end": v(34.03, -33.87) * mm});
            skLineSegment(sketch, "E355", {"start": v(34.03, -33.87) * mm, "end": v(34.4, -34.1) * mm});
            skLineSegment(sketch, "E356", {"start": v(34.4, -34.1) * mm, "end": v(34.85, -34.37) * mm});
            skLineSegment(sketch, "E357", {"start": v(34.85, -34.37) * mm, "end": v(35.4, -34.66) * mm});
            skLineSegment(sketch, "E358", {"start": v(35.4, -34.66) * mm, "end": v(36.04, -34.96) * mm});
            skLineSegment(sketch, "E359", {"start": v(36.04, -34.96) * mm, "end": v(36.78, -35.27) * mm});
            skLineSegment(sketch, "E360", {"start": v(36.78, -35.27) * mm, "end": v(37.62, -35.58) * mm});
            skLineSegment(sketch, "E361", {"start": v(37.62, -35.58) * mm, "end": v(38.55, -35.88) * mm});
            skLineSegment(sketch, "E362", {"start": v(38.55, -35.88) * mm, "end": v(39.58, -36.16) * mm});
            skLineSegment(sketch, "E363", {"start": v(39.58, -36.16) * mm, "end": v(40.7, -36.41) * mm});
            skLineSegment(sketch, "E364", {"start": v(40.7, -36.41) * mm, "end": v(41.93, -36.64) * mm});
            skLineSegment(sketch, "E365", {"start": v(41.93, -36.64) * mm, "end": v(43.26, -36.82) * mm});
            skLineSegment(sketch, "E366", {"start": v(43.26, -36.82) * mm, "end": v(44.68, -36.95) * mm});
            skLineSegment(sketch, "E367", {"start": v(44.68, -36.95) * mm, "end": v(46.2, -37.02) * mm});
            skLineSegment(sketch, "E368", {"start": v(46.2, -37.02) * mm, "end": v(47.8, -37.03) * mm});
            skLineSegment(sketch, "E369", {"start": v(47.8, -37.03) * mm, "end": v(49.5, -36.96) * mm});
            skLineSegment(sketch, "E370", {"start": v(49.5, -36.96) * mm, "end": v(51.28, -36.81) * mm});
            skLineSegment(sketch, "E371", {"start": v(51.28, -36.81) * mm, "end": v(53.14, -36.57) * mm});
            skLineSegment(sketch, "E372", {"start": v(53.14, -36.57) * mm, "end": v(55.08, -36.24) * mm});
            skLineSegment(sketch, "E373", {"start": v(55.08, -36.24) * mm, "end": v(56.04, -35.15) * mm});
            skLineSegment(sketch, "E374", {"start": v(56.04, -35.15) * mm, "end": v(56.52, -34.36) * mm});
            skLineSegment(sketch, "E375", {"start": v(56.52, -34.36) * mm, "end": v(57.07, -33.01) * mm});
            skLineSegment(sketch, "E376", {"start": v(57.07, -33.01) * mm, "end": v(56.5, -31.13) * mm});
            skLineSegment(sketch, "E377", {"start": v(56.5, -31.13) * mm, "end": v(55.88, -29.36) * mm});
            skLineSegment(sketch, "E378", {"start": v(55.88, -29.36) * mm, "end": v(55.21, -27.7) * mm});
            skLineSegment(sketch, "E379", {"start": v(55.21, -27.7) * mm, "end": v(54.51, -26.16) * mm});
            skLineSegment(sketch, "E380", {"start": v(54.51, -26.16) * mm, "end": v(53.79, -24.72) * mm});
            skLineSegment(sketch, "E381", {"start": v(53.79, -24.72) * mm, "end": v(53.04, -23.4) * mm});
            skLineSegment(sketch, "E382", {"start": v(53.04, -23.4) * mm, "end": v(52.3, -22.2) * mm});
            skLineSegment(sketch, "E383", {"start": v(52.3, -22.2) * mm, "end": v(51.54, -21.09) * mm});
            skLineSegment(sketch, "E384", {"start": v(51.54, -21.09) * mm, "end": v(50.79, -20.09) * mm});
            skLineSegment(sketch, "E385", {"start": v(50.79, -20.09) * mm, "end": v(50.05, -19.2) * mm});
            skLineSegment(sketch, "E386", {"start": v(50.05, -19.2) * mm, "end": v(49.34, -18.4) * mm});
            skLineSegment(sketch, "E387", {"start": v(49.34, -18.4) * mm, "end": v(48.66, -17.7) * mm});
            skLineSegment(sketch, "E388", {"start": v(48.66, -17.7) * mm, "end": v(48.01, -17.09) * mm});
            skLineSegment(sketch, "E389", {"start": v(48.01, -17.09) * mm, "end": v(47.4, -16.57) * mm});
            skLineSegment(sketch, "E390", {"start": v(47.4, -16.57) * mm, "end": v(46.85, -16.13) * mm});
            skLineSegment(sketch, "E391", {"start": v(46.85, -16.13) * mm, "end": v(46.34, -15.77) * mm});
            skLineSegment(sketch, "E392", {"start": v(46.34, -15.77) * mm, "end": v(45.9, -15.48) * mm});
            skLineSegment(sketch, "E393", {"start": v(45.9, -15.48) * mm, "end": v(45.52, -15.25) * mm});
            skLineSegment(sketch, "E394", {"start": v(45.52, -15.25) * mm, "end": v(45.21, -15.09) * mm});
            skLineSegment(sketch, "E395", {"start": v(45.21, -15.09) * mm, "end": v(44.98, -14.97) * mm});
            skLineSegment(sketch, "E396", {"start": v(44.98, -14.97) * mm, "end": v(44.82, -14.9) * mm});
            skLineSegment(sketch, "E397", {"start": v(44.82, -14.9) * mm, "end": v(44.75, -14.88) * mm});
            skLineSegment(sketch, "E398", {"start": v(44.75, -14.88) * mm, "end": v(35.78, -11.9) * mm});
            skLineSegment(sketch, "E399", {"start": v(35.78, -11.9) * mm, "end": v(37.7, 0) * mm});
            skLineSegment(sketch, "E400", {"start": v(2.65, 0) * mm, "end": v(-2.65, 0) * mm});
            skLineSegment(sketch, "E401", {"start": v(0, -2.65) * mm, "end": v(0, 2.65) * mm});
            skLineSegment(sketch, "E402", {"start": v(56.69, 12.18) * mm, "end": v(56.69, 11.92) * mm});
            skLineSegment(sketch, "E403", {"start": v(56.69, 11.92) * mm, "end": v(56.58, 11.13) * mm});
            skLineSegment(sketch, "E404", {"start": v(56.58, 11.13) * mm, "end": v(56.28, 10.16) * mm});
            skLineSegment(sketch, "E405", {"start": v(56.28, 10.16) * mm, "end": v(55.8, 9.27) * mm});
            skLineSegment(sketch, "E406", {"start": v(55.8, 9.27) * mm, "end": v(55.17, 8.5) * mm});
            skLineSegment(sketch, "E407", {"start": v(55.17, 8.5) * mm, "end": v(54.4, 7.87) * mm});
            skLineSegment(sketch, "E408", {"start": v(54.4, 7.87) * mm, "end": v(53.52, 7.4) * mm});
            skLineSegment(sketch, "E409", {"start": v(53.52, 7.4) * mm, "end": v(52.54, 7.1) * mm});
            skLineSegment(sketch, "E410", {"start": v(52.54, 7.1) * mm, "end": v(51.76, 6.98) * mm});
            skLineSegment(sketch, "E411", {"start": v(51.76, 6.98) * mm, "end": v(51.5, 6.98) * mm});
            skLineSegment(sketch, "E412", {"start": v(51.5, 6.98) * mm, "end": v(51.24, 6.98) * mm});
            skLineSegment(sketch, "E413", {"start": v(51.24, 6.98) * mm, "end": v(50.45, 7.1) * mm});
            skLineSegment(sketch, "E414", {"start": v(50.45, 7.1) * mm, "end": v(49.48, 7.4) * mm});
            skLineSegment(sketch, "E415", {"start": v(49.48, 7.4) * mm, "end": v(48.6, 7.87) * mm});
            skLineSegment(sketch, "E416", {"start": v(48.6, 7.87) * mm, "end": v(47.82, 8.5) * mm});
            skLineSegment(sketch, "E417", {"start": v(47.82, 8.5) * mm, "end": v(47.2, 9.27) * mm});
            skLineSegment(sketch, "E418", {"start": v(47.2, 9.27) * mm, "end": v(46.71, 10.16) * mm});
            skLineSegment(sketch, "E419", {"start": v(46.71, 10.16) * mm, "end": v(46.4, 11.13) * mm});
            skLineSegment(sketch, "E420", {"start": v(46.4, 11.13) * mm, "end": v(46.3, 11.92) * mm});
            skLineSegment(sketch, "E421", {"start": v(46.3, 11.92) * mm, "end": v(46.3, 12.18) * mm});
            skLineSegment(sketch, "E422", {"start": v(46.3, 12.18) * mm, "end": v(46.3, 12.44) * mm});
            skLineSegment(sketch, "E423", {"start": v(46.3, 12.44) * mm, "end": v(46.4, 13.22) * mm});
            skLineSegment(sketch, "E424", {"start": v(46.4, 13.22) * mm, "end": v(46.71, 14.2) * mm});
            skLineSegment(sketch, "E425", {"start": v(46.71, 14.2) * mm, "end": v(47.2, 15.08) * mm});
            skLineSegment(sketch, "E426", {"start": v(47.2, 15.08) * mm, "end": v(47.82, 15.85) * mm});
            skLineSegment(sketch, "E427", {"start": v(47.82, 15.85) * mm, "end": v(48.6, 16.48) * mm});
            skLineSegment(sketch, "E428", {"start": v(48.6, 16.48) * mm, "end": v(49.48, 16.96) * mm});
            skLineSegment(sketch, "E429", {"start": v(49.48, 16.96) * mm, "end": v(50.45, 17.26) * mm});
            skLineSegment(sketch, "E430", {"start": v(50.45, 17.26) * mm, "end": v(51.24, 17.37) * mm});
            skLineSegment(sketch, "E431", {"start": v(51.24, 17.37) * mm, "end": v(51.5, 17.37) * mm});
            skLineSegment(sketch, "E432", {"start": v(51.5, 17.37) * mm, "end": v(51.76, 17.37) * mm});
            skLineSegment(sketch, "E433", {"start": v(51.76, 17.37) * mm, "end": v(52.54, 17.26) * mm});
            skLineSegment(sketch, "E434", {"start": v(52.54, 17.26) * mm, "end": v(53.52, 16.96) * mm});
            skLineSegment(sketch, "E435", {"start": v(53.52, 16.96) * mm, "end": v(54.4, 16.48) * mm});
            skLineSegment(sketch, "E436", {"start": v(54.4, 16.48) * mm, "end": v(55.17, 15.85) * mm});
            skLineSegment(sketch, "E437", {"start": v(55.17, 15.85) * mm, "end": v(55.8, 15.08) * mm});
            skLineSegment(sketch, "E438", {"start": v(55.8, 15.08) * mm, "end": v(56.28, 14.2) * mm});
            skLineSegment(sketch, "E439", {"start": v(56.28, 14.2) * mm, "end": v(56.58, 13.22) * mm});
            skLineSegment(sketch, "E440", {"start": v(56.58, 13.22) * mm, "end": v(56.69, 12.44) * mm});
            skLineSegment(sketch, "E441", {"start": v(56.69, 12.44) * mm, "end": v(56.69, 12.18) * mm});
            skSolve(sketch);
        }
        {
            var Q0;
            Q0=makeQuery(id+"F0.imprint","IMPRINT",FACE,{"disambiguationData":[TD([[makeQuery(id+"F0.imprint","IMPRINT",EDGE,{"derivedFrom":sQuery(id+"F0.wireOp",EDGE,"E0")}),1.0]])]});
            extrude(context, id + "F1", {"entities" : qUnion([Q0]), "depth" : 25.4 * mm, "offsetDistance" : 25.4 * mm});
        }
    });
